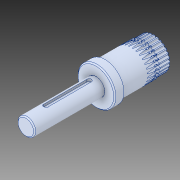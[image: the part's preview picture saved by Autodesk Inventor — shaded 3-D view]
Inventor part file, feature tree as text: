
AUTODESK INVENTOR PART (.ipt)
format: ipt  version: 2019 (Build 230136000, 136)  size: 1,410,560 bytes
history: native  units: in
note: dims shown in document units (in); Inventor stores cm internally (conversion verified against a paired STEP export)
features: other x1, chamfer x1
ambient origin geometry x8: Origin, YZ Plane, XZ Plane, XY Plane, X Axis, Y Axis, Z Axis, Center Point
bodies: Solid1 (feature_tree), Solid2 (feature_tree)
feature tree (2):
  other  "8MM CIM SHAFT"
  chamfer  "Chamfer3"  [1 undecoded]
note: 1 required parameter value undecoded (feature->parameter linkage not recoverable at this tier; creation-order binding heuristic only, values carry confidence <= 0.55)
